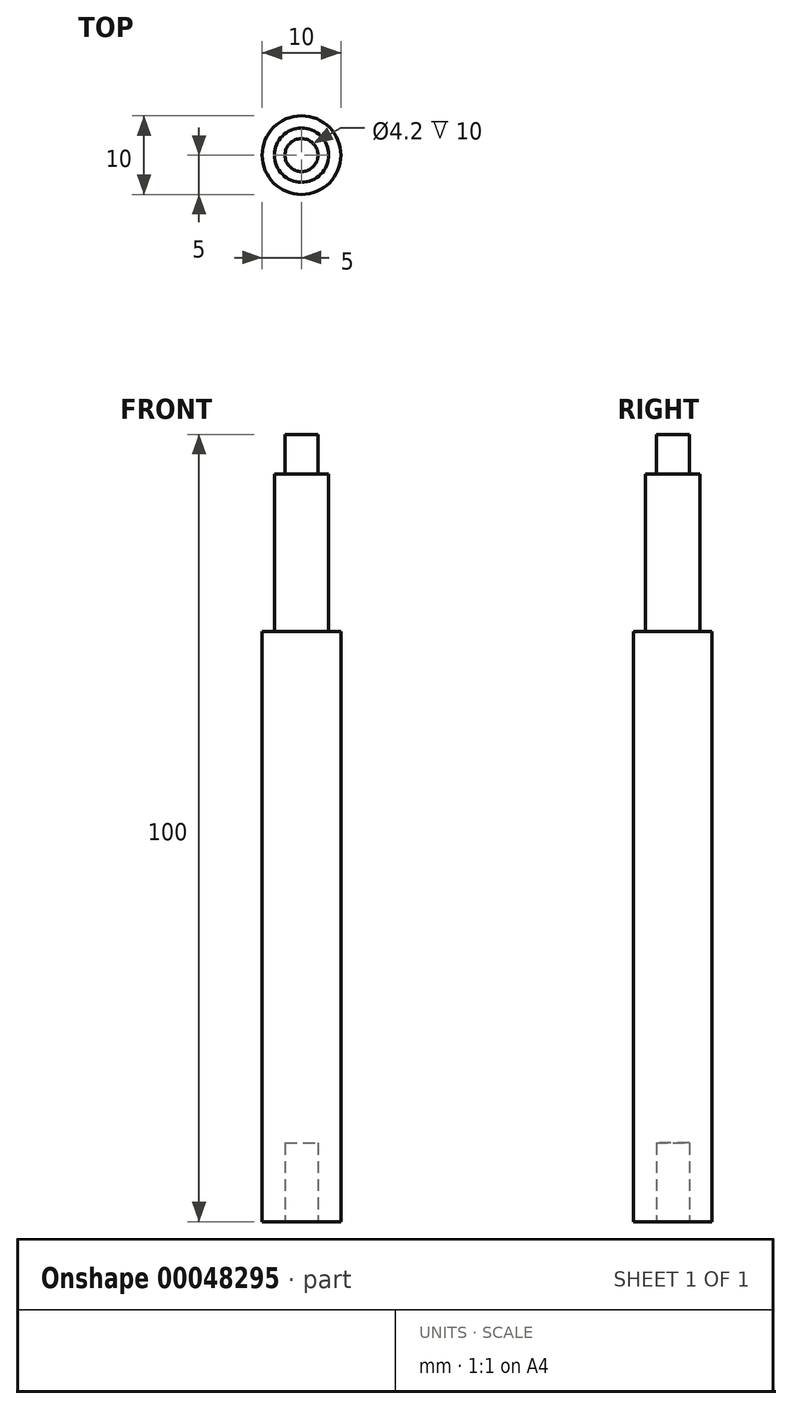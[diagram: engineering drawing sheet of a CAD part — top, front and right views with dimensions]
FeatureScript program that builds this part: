
annotation { "Feature Type Name" : "Feature", "Feature Type Description" : "" }
export const myFeature = defineFeature(function(context is Context, id is Id, definition is map)
    precondition{}
    {
        {
            var Q0;
            Q0=qCreatedBy(makeId("Top.planeOp"),FACE);
            var sketch = newSketch(context, id + "F0", { "sketchPlane" : qUnion([Q0])});
            skCircle(sketch, "E0", {"center": v(0, 0) * mm, "radius": 5 * mm});
            skSolve(sketch);
        }
        {
            var Q0;
            Q0=makeQuery(id+"F0.imprint","IMPRINT",FACE,{"disambiguationData":[TD([[makeQuery(id+"F0.imprint","IMPRINT",EDGE,{"derivedFrom":sQuery(id+"F0.wireOp",EDGE,"E0")}),1.0]])]});
            extrude(context, id + "F1", {"entities" : qUnion([Q0]), "depth" : 75 * mm});
        }
        {
            var Q0;
            Q0=makeQuery(id+"F1.opExtrude","CAP_FACE",FACE,{"disambiguationData":[OSD([sQuery(id+"F0.wireOp",EDGE,"E0")])],"isStart":false});
            var sketch = newSketch(context, id + "F2", { "sketchPlane" : qUnion([Q0])});
            skCircle(sketch, "E1", {"center": v(0, 0) * mm, "radius": 3.45 * mm});
            skSolve(sketch);
        }
        {
            var Q0;
            Q0=makeQuery(id+"F2.imprint","IMPRINT",FACE,{"disambiguationData":[TD([[makeQuery(id+"F2.imprint","IMPRINT",EDGE,{"derivedFrom":sQuery(id+"F2.wireOp",EDGE,"E1")}),1.0]])]});
            extrude(context, id + "F3", {"entities" : qUnion([Q0]), "operationType" : NewBodyOperationType.ADD, "depth" : 20 * mm});
        }
        {
            var Q0;
            Q0=makeQuery(id+"F3.opExtrude","CAP_FACE",FACE,{"disambiguationData":[OSD([sQuery(id+"F2.wireOp",EDGE,"E1")])],"isStart":false});
            var sketch = newSketch(context, id + "F4", { "sketchPlane" : qUnion([Q0])});
            skCircle(sketch, "E2", {"center": v(0, 0) * mm, "radius": 2.1 * mm});
            skSolve(sketch);
        }
        {
            var Q0;
            Q0=makeQuery(id+"F4.imprint","IMPRINT",FACE,{"disambiguationData":[TD([[makeQuery(id+"F4.imprint","IMPRINT",EDGE,{"derivedFrom":sQuery(id+"F4.wireOp",EDGE,"E2")}),1.0]])]});
            extrude(context, id + "F5", {"entities" : qUnion([Q0]), "operationType" : NewBodyOperationType.ADD, "depth" : 5 * mm});
        }
        {
            var Q0;
            Q0=makeQuery(id+"F1.opExtrude","CAP_FACE",FACE,{"disambiguationData":[OSD([sQuery(id+"F0.wireOp",EDGE,"E0")])],"isStart":true});
            var sketch = newSketch(context, id + "F6", { "sketchPlane" : qUnion([Q0])});
            skCircle(sketch, "E3", {"center": v(0, 0) * mm, "radius": 2.1 * mm});
            skSolve(sketch);
        }
        {
            var Q0;
            Q0=makeQuery(id+"F6.imprint","IMPRINT",FACE,{"disambiguationData":[TD([[makeQuery(id+"F6.imprint","IMPRINT",EDGE,{"derivedFrom":sQuery(id+"F6.wireOp",EDGE,"E3")}),1.0]])]});
            extrude(context, id + "F7", {"entities" : qUnion([Q0]), "operationType" : NewBodyOperationType.REMOVE, "oppositeDirection" : true, "depth" : 10 * mm});
        }
    });
